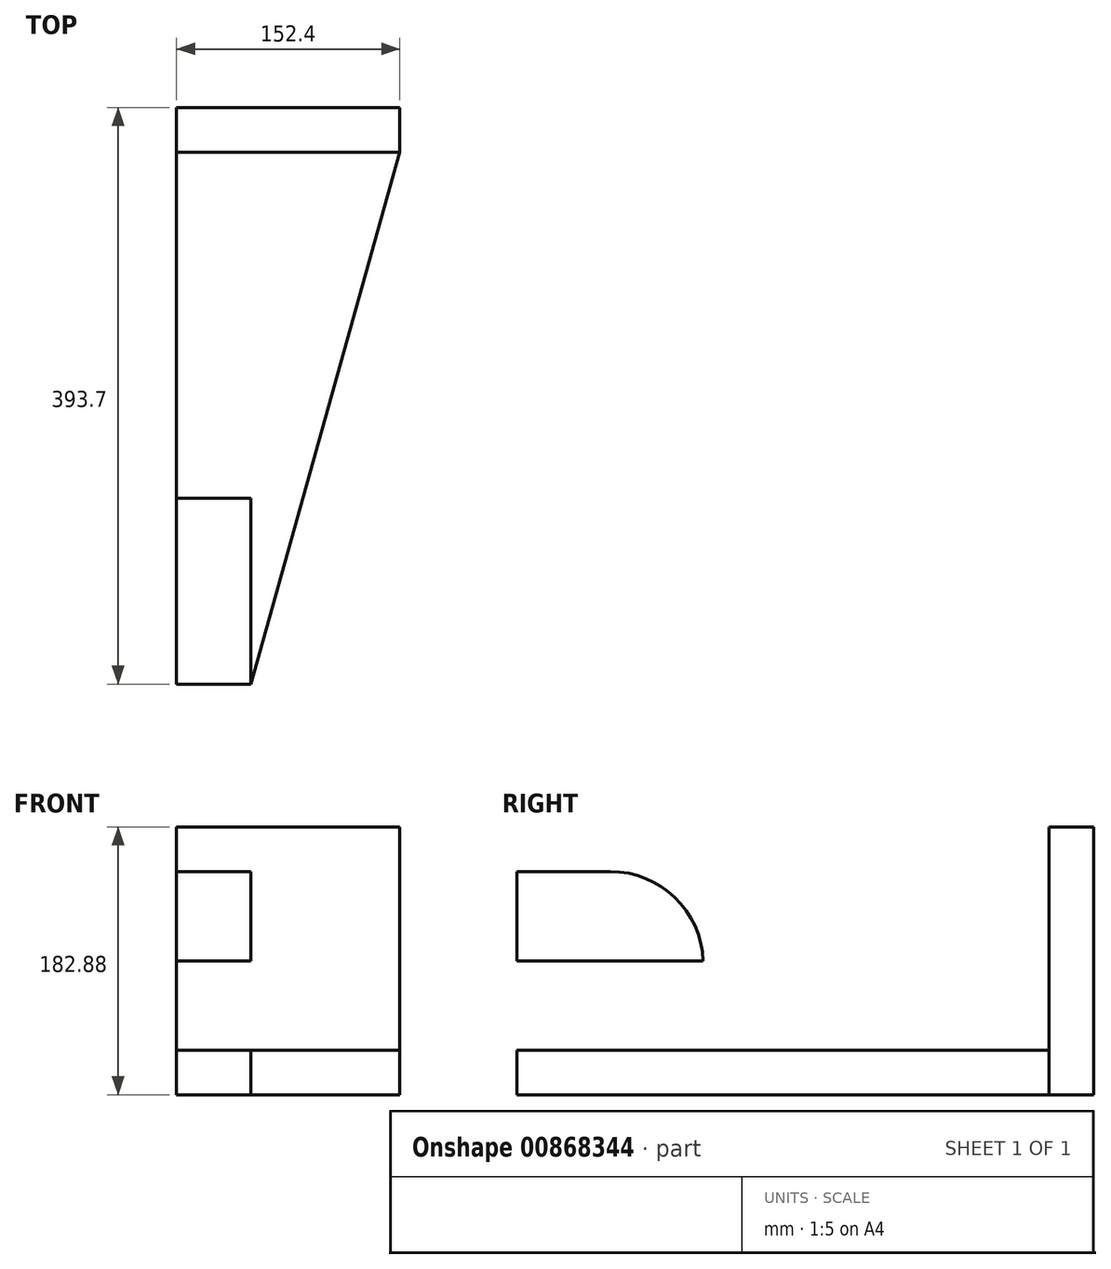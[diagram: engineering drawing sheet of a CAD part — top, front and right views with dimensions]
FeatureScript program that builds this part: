
annotation { "Feature Type Name" : "Feature", "Feature Type Description" : "" }
export const myFeature = defineFeature(function(context is Context, id is Id, definition is map)
    precondition{}
    {
        {
            var Q0;
            Q0=qCreatedBy(makeId("Top.planeOp"),FACE);
            var sketch = newSketch(context, id + "F0", { "sketchPlane" : qUnion([Q0])});
            skLineSegment(sketch, "E0.bottom", {"start": v(0, 0) * mm, "end": v(152.4, 0) * mm});
            skLineSegment(sketch, "E0.top", {"start": v(0, -393.7) * mm, "end": v(152.4, -393.7) * mm});
            skLineSegment(sketch, "E0.left", {"start": v(0, 0) * mm, "end": v(0, -393.7) * mm});
            skLineSegment(sketch, "E0.right", {"start": v(152.4, 0) * mm, "end": v(152.4, -393.7) * mm});
            skLineSegment(sketch, "E1", {"start": v(0, -393.7) * mm, "end": v(50.8, -393.7) * mm});
            skLineSegment(sketch, "E2", {"start": v(152.4, 0) * mm, "end": v(50.8, -393.7) * mm});
            skSolve(sketch);
        }
        {
            var Q0;
            Q0=makeQuery(id+"F0.imprint","IMPRINT",FACE,{"disambiguationData":[TD([[makeQuery(id+"F0.imprint","IMPRINT",EDGE,{"derivedFrom":sQuery(id+"F0.wireOp",EDGE,"E0.bottom")}),-1.0]])]});
            extrude(context, id + "F1", {"entities" : qUnion([Q0]), "depth" : 30.48 * mm, "offsetDistance" : 25.4 * mm});
        }
        {
            var Q0;
            Q0=makeQuery(id+"F1.opExtrude","CAP_FACE",FACE,{"disambiguationData":[OSD([sQuery(id+"F0.wireOp",EDGE,"E0.bottom"),sQuery(id+"F0.wireOp",EDGE,"E0.left"),sQuery(id+"F0.wireOp",EDGE,"E1"),sQuery(id+"F0.wireOp",EDGE,"E2")])],"isStart":false});
            var sketch = newSketch(context, id + "F2", { "sketchPlane" : qUnion([Q0])});
            skLineSegment(sketch, "E3", {"start": v(0, 0) * mm, "end": v(0, -30.48) * mm});
            skLineSegment(sketch, "E4", {"start": v(0, -30.48) * mm, "end": v(152.4, -30.48) * mm});
            skLineSegment(sketch, "E5", {"start": v(152.4, -30.48) * mm, "end": v(152.4, 0) * mm});
            skSolve(sketch);
        }
        {
            var Q0;
            {var subQ0=sQuery(id+"F2.wireOp",EDGE,"E5");Q0=makeQuery(id+"F2.imprint","IMPRINT",FACE,{"disambiguationData":[TD([[makeQuery(id+"F2.imprint","IMPRINT",EDGE,{"derivedFrom":subQ0}),1.0]])]});}
            extrude(context, id + "F3", {"entities" : qUnion([Q0]), "operationType" : NewBodyOperationType.ADD, "oppositeDirection" : true, "depth" : 30.48 * mm, "offsetDistance" : 25.4 * mm});
        }
        {
            var Q0;
            {var subQ0=sQuery(id+"F0.wireOp",EDGE,"E2");Q0=makeQuery(id+"F3.boolean.opBoolean","MERGE",FACE,{"derivedFrom":[makeQuery(id+"F1.opExtrude","CAP_FACE",FACE,{"disambiguationData":[OSD([sQuery(id+"F0.wireOp",EDGE,"E0.bottom"),sQuery(id+"F0.wireOp",EDGE,"E0.left"),sQuery(id+"F0.wireOp",EDGE,"E1"),subQ0])],"isStart":false}),makeQuery(id+"F3.opExtrude","CAP_FACE",FACE,{"disambiguationData":[OSD([subQ0,sQuery(id+"F2.wireOp",EDGE,"E4"),sQuery(id+"F2.wireOp",EDGE,"E5")])],"isStart":true})]});}
            var sketch = newSketch(context, id + "F4", { "sketchPlane" : qUnion([Q0])});
            skLineSegment(sketch, "E6", {"start": v(152.4, -30.48) * mm, "end": v(50.8, -393.7) * mm});
            skSolve(sketch);
        }
        {
            var Q0;
            Q0=makeQuery(id+"F4.imprint","IMPRINT",FACE,{"disambiguationData":[TD([[makeQuery(id+"F4.imprint","IMPRINT",EDGE,{"derivedFrom":sQuery(id+"F4.wireOp",EDGE,"E6")}),-1.0]])]});
            extrude(context, id + "F5", {"entities" : qUnion([Q0]), "operationType" : NewBodyOperationType.ADD, "oppositeDirection" : true, "depth" : 30.48 * mm, "offsetDistance" : 25.4 * mm});
        }
        {
            var Q0;
            {var subQ0=sQuery(id+"F2.wireOp",EDGE,"E4");var subQ1=sQuery(id+"F0.wireOp",EDGE,"E2");Q0=makeQuery(id+"F5.boolean.opBoolean","MERGE",FACE,{"derivedFrom":[makeQuery(id+"F3.boolean.opBoolean","MERGE",FACE,{"derivedFrom":[makeQuery(id+"F1.opExtrude","CAP_FACE",FACE,{"disambiguationData":[OSD([sQuery(id+"F0.wireOp",EDGE,"E0.bottom"),sQuery(id+"F0.wireOp",EDGE,"E0.left"),sQuery(id+"F0.wireOp",EDGE,"E1"),subQ1])],"isStart":false}),makeQuery(id+"F3.opExtrude","CAP_FACE",FACE,{"disambiguationData":[OSD([subQ1,subQ0,sQuery(id+"F2.wireOp",EDGE,"E5")])],"isStart":true})]}),makeQuery(id+"F5.opExtrude","CAP_FACE",FACE,{"disambiguationData":[OSD([subQ1,subQ0,sQuery(id+"F4.wireOp",EDGE,"E6")])],"isStart":true})]});}
            var sketch = newSketch(context, id + "F6", { "sketchPlane" : qUnion([Q0])});
            skLineSegment(sketch, "E7", {"start": v(152.4, -30.48) * mm, "end": v(0, -30.48) * mm});
            skSolve(sketch);
        }
        {
            var Q0;
            {var subQ0=sQuery(id+"F6.wireOp",EDGE,"E7");Q0=makeQuery(id+"F6.imprint","IMPRINT",FACE,{"disambiguationData":[TD([[makeQuery(id+"F6.imprint","IMPRINT",EDGE,{"derivedFrom":subQ0}),-1.0]])]});}
            extrude(context, id + "F7", {"entities" : qUnion([Q0]), "operationType" : NewBodyOperationType.ADD, "depth" : 152.4 * mm, "offsetDistance" : 25.4 * mm});
        }
        {
            var Q0;
            {var subQ0=sQuery(id+"F2.wireOp",EDGE,"E4");var subQ1=sQuery(id+"F0.wireOp",EDGE,"E2");Q0=makeQuery(id+"F5.boolean.opBoolean","MERGE",FACE,{"derivedFrom":[makeQuery(id+"F3.boolean.opBoolean","MERGE",FACE,{"derivedFrom":[makeQuery(id+"F1.opExtrude","CAP_FACE",FACE,{"disambiguationData":[OSD([sQuery(id+"F0.wireOp",EDGE,"E0.bottom"),sQuery(id+"F0.wireOp",EDGE,"E0.left"),sQuery(id+"F0.wireOp",EDGE,"E1"),subQ1])],"isStart":false}),makeQuery(id+"F3.opExtrude","CAP_FACE",FACE,{"disambiguationData":[OSD([subQ1,subQ0,sQuery(id+"F2.wireOp",EDGE,"E5")])],"isStart":true})]}),makeQuery(id+"F5.opExtrude","CAP_FACE",FACE,{"disambiguationData":[OSD([subQ1,subQ0,sQuery(id+"F4.wireOp",EDGE,"E6")])],"isStart":true})]});}
            var sketch = newSketch(context, id + "F8", { "sketchPlane" : qUnion([Q0])});
            skLineSegment(sketch, "E8", {"start": v(50.8, -393.7) * mm, "end": v(50.8, -266.7) * mm});
            skLineSegment(sketch, "E9", {"start": v(0, -266.7) * mm, "end": v(50.8, -266.7) * mm});
            skSolve(sketch);
        }
        {
            var Q0;
            Q0=makeQuery(id+"F8.imprint","IMPRINT",FACE,{"disambiguationData":[TD([[makeQuery(id+"F8.imprint","IMPRINT",EDGE,{"derivedFrom":sQuery(id+"F8.wireOp",EDGE,"E8")}),1.0]])]});
            extrude(context, id + "F9", {"entities" : qUnion([Q0]), "operationType" : NewBodyOperationType.ADD, "depth" : 121.92 * mm, "offsetDistance" : 25.4 * mm});
        }
        {
            var Q0;
            Q0=makeQuery(id+"F9.opExtrude","SWEPT_FACE",FACE,{"disambiguationData":[OSD([sQuery(id+"F8.wireOp",EDGE,"E8")])]});
            var sketch = newSketch(context, id + "F10", { "sketchPlane" : qUnion([Q0])});
            skLineSegment(sketch, "E10", {"start": v(-266.7, 152.4) * mm, "end": v(-393.7, 152.4) * mm});
            skLineSegment(sketch, "E11", {"start": v(-393.7, 152.4) * mm, "end": v(-330.2, 152.4) * mm});
            skLineSegment(sketch, "E12", {"start": v(-330.2, 152.4) * mm, "end": v(-330.2, 30.48) * mm});
            skLineSegment(sketch, "E13", {"start": v(-330.2, 30.48) * mm, "end": v(-266.7, 30.48) * mm});
            skLineSegment(sketch, "E14", {"start": v(-266.7, 30.48) * mm, "end": v(-266.7, 152.4) * mm});
            skLineSegment(sketch, "E15", {"start": v(-393.7, 152.4) * mm, "end": v(-393.7, 30.48) * mm});
            skLineSegment(sketch, "E16", {"start": v(-393.7, 30.48) * mm, "end": v(-330.2, 30.48) * mm});
            skLineSegment(sketch, "E17", {"start": v(-393.7, 91.44) * mm, "end": v(-266.7, 91.44) * mm});
            skCircle(sketch, "E18", {"center": v(-330.2, 91.44) * mm, "radius": 31.75 * mm});
            skSolve(sketch);
        }
        {
            var Q0;
            {var subQ0=sQuery(id+"F10.wireOp",EDGE,"E18");var subQ1=sQuery(id+"F10.wireOp",EDGE,"E12");var subQ2=makeQuery(id+"F10.imprint","INTERSECT",VERTEX,{"disambiguationData":[OD(0.0)],"derivedFrom":[subQ1,subQ0]});Q0=makeQuery(id+"F10.imprint","IMPRINT",FACE,{"disambiguationData":[TD([[makeQuery(id+"F10.imprint","IMPRINT",EDGE,{"disambiguationData":[TD([[subQ2,-1.0]])],"derivedFrom":subQ1}),-1.0]])]});}
            var Q1;
            {var subQ0=sQuery(id+"F10.wireOp",EDGE,"E18");var subQ1=sQuery(id+"F10.wireOp",EDGE,"E12");var subQ2=makeQuery(id+"F10.imprint","INTERSECT",VERTEX,{"disambiguationData":[OD(0.0)],"derivedFrom":[subQ1,subQ0]});Q1=makeQuery(id+"F10.imprint","IMPRINT",FACE,{"disambiguationData":[TD([[makeQuery(id+"F10.imprint","IMPRINT",EDGE,{"disambiguationData":[TD([[subQ2,-1.0]])],"derivedFrom":subQ1}),1.0]])]});}
            var Q2;
            {var subQ0=sQuery(id+"F10.wireOp",EDGE,"E17");var subQ1=sQuery(id+"F10.wireOp",EDGE,"E12");var subQ2=makeQuery(id+"F10.imprint","INTERSECT",VERTEX,{"derivedFrom":[subQ1,subQ0]});Q2=makeQuery(id+"F10.imprint","IMPRINT",FACE,{"disambiguationData":[TD([[makeQuery(id+"F10.imprint","IMPRINT",EDGE,{"disambiguationData":[TD([[subQ2,-1.0]])],"derivedFrom":subQ1}),-1.0]])]});}
            var Q3;
            {var subQ0=sQuery(id+"F10.wireOp",EDGE,"E17");var subQ1=sQuery(id+"F10.wireOp",EDGE,"E12");var subQ2=makeQuery(id+"F10.imprint","INTERSECT",VERTEX,{"derivedFrom":[subQ1,subQ0]});Q3=makeQuery(id+"F10.imprint","IMPRINT",FACE,{"disambiguationData":[TD([[makeQuery(id+"F10.imprint","IMPRINT",EDGE,{"disambiguationData":[TD([[subQ2,-1.0]])],"derivedFrom":subQ1}),1.0]])]});}
            extrude(context, id + "F11", {"entities" : qUnion([Q0, Q1, Q2, Q3]), "operationType" : NewBodyOperationType.REMOVE, "oppositeDirection" : true, "depth" : 475.74 * mm, "offsetDistance" : 25.4 * mm});
        }
        {
            var Q0;
            Q0=makeQuery(id+"F9.opExtrude","CAP_EDGE",EDGE,{"disambiguationData":[OSD([sQuery(id+"F0.wireOp",EDGE,"E1")])],"isStart":false});
            var Q1;
            Q1=makeQuery(id+"F9.opExtrude","CAP_EDGE",EDGE,{"disambiguationData":[OSD([sQuery(id+"F8.wireOp",EDGE,"E9")])],"isStart":false});
            fillet(context, id + "F12", {"entities" : qUnion([Q0, Q1]), "radius" : 63.5 * mm, "tangentPropagation" : true, "allowEdgeOverflow" : false});
        }
    });
